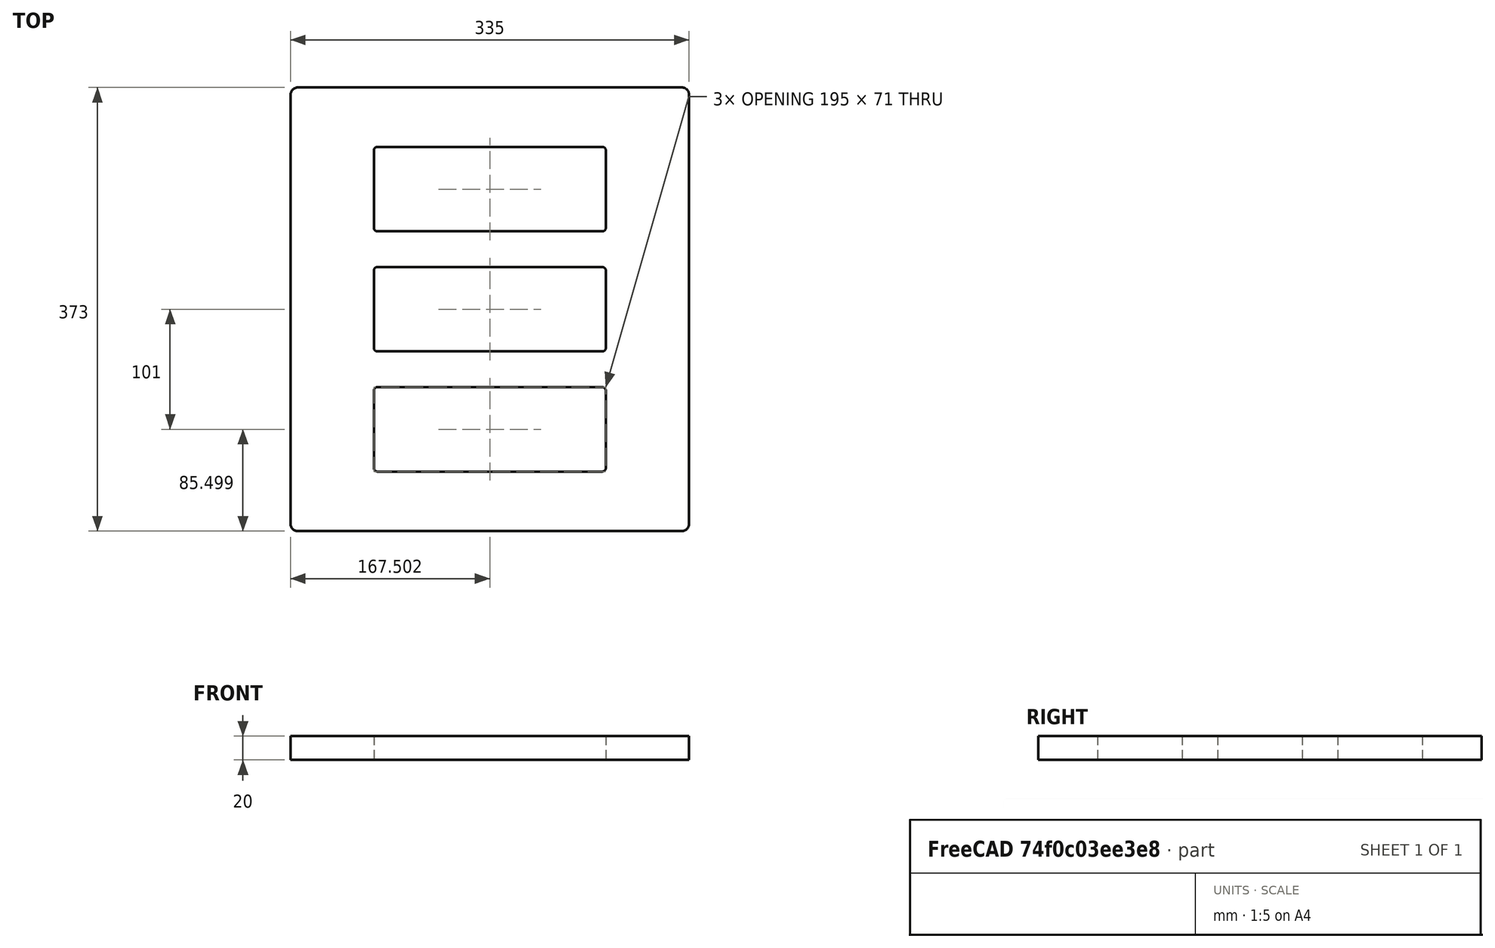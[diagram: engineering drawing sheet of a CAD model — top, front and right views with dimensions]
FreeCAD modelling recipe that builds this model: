
FCSTD DOCUMENT  (FreeCAD 0.16R6706 (Git))
Label: model
License: All rights reserved
LicenseURL: http://en.wikipedia.org/wiki/All_rights_reserved
objects: Sketcher::SketchObject×1, PartDesign::Pad×1
note: 3 computed .brp shape members not serialized (recipe doc carries the construction recipe); baked Part::Feature solids carry a one-line shape summary decoded from their .brp

FEATURE [Sketcher::SketchObject] Sketch002
  sketch-geometry (32):
    g0: LineSegment StartX=78.4625 StartY=-38.9411 StartZ=0 EndX=267.462 EndY=-38.9411 EndZ=0
    g1: LineSegment StartX=270.462 StartY=-41.9411 StartZ=0 EndX=270.462 EndY=-106.941 EndZ=0
    g2: LineSegment StartX=267.462 StartY=-109.941 StartZ=0 EndX=78.4625 EndY=-109.941 EndZ=0
    g3: LineSegment StartX=75.4625 StartY=-106.941 StartZ=0 EndX=75.4625 EndY=-41.9411 EndZ=0
    g4: LineSegment StartX=11.4625 StartY=11.0589 StartZ=0 EndX=334.462 EndY=11.0589 EndZ=0
    g5: LineSegment StartX=340.462 StartY=5.05895 StartZ=0 EndX=340.462 EndY=-355.941 EndZ=0
    g6: LineSegment StartX=334.462 StartY=-361.941 StartZ=0 EndX=11.4625 EndY=-361.941 EndZ=0
    g7: LineSegment StartX=5.46248 StartY=-355.941 StartZ=0 EndX=5.46248 EndY=5.05895 EndZ=0
    g8: ArcOfCircle CenterX=78.4625 CenterY=-41.9411 CenterZ=0 NormalX=0 NormalY=0 NormalZ=1 Radius=3 StartAngle=1.5708 EndAngle=3.14159
    g9: ArcOfCircle CenterX=78.4625 CenterY=-106.941 CenterZ=0 NormalX=0 NormalY=0 NormalZ=1 Radius=3 StartAngle=3.14159 EndAngle=4.71239
    g10: ArcOfCircle CenterX=267.462 CenterY=-106.941 CenterZ=0 NormalX=0 NormalY=0 NormalZ=1 Radius=3 StartAngle=4.71239 EndAngle=6.28319
    g11: ArcOfCircle CenterX=267.462 CenterY=-41.9411 CenterZ=0 NormalX=0 NormalY=0 NormalZ=1 Radius=3 StartAngle=0 EndAngle=1.5708
    g12: ArcOfCircle CenterX=334.462 CenterY=5.05895 CenterZ=0 NormalX=0 NormalY=0 NormalZ=1 Radius=6 StartAngle=0 EndAngle=1.5708
    g13: ArcOfCircle CenterX=11.4625 CenterY=5.05895 CenterZ=0 NormalX=0 NormalY=0 NormalZ=1 Radius=6 StartAngle=1.5708 EndAngle=3.14159
    g14: ArcOfCircle CenterX=11.4625 CenterY=-355.941 CenterZ=0 NormalX=0 NormalY=0 NormalZ=1 Radius=6 StartAngle=3.14159 EndAngle=4.71239
    g15: ArcOfCircle CenterX=334.462 CenterY=-355.941 CenterZ=0 NormalX=0 NormalY=0 NormalZ=1 Radius=6 StartAngle=4.71239 EndAngle=6.28319
    g16: LineSegment StartX=78.4625 StartY=-139.941 StartZ=0 EndX=267.462 EndY=-139.941 EndZ=0
    g17: LineSegment StartX=270.462 StartY=-142.941 StartZ=0 EndX=270.462 EndY=-207.941 EndZ=0
    g18: LineSegment StartX=267.462 StartY=-210.941 StartZ=0 EndX=78.4625 EndY=-210.941 EndZ=0
    g19: LineSegment StartX=75.4625 StartY=-207.941 StartZ=0 EndX=75.4625 EndY=-142.941 EndZ=0
    g20: LineSegment StartX=78.4625 StartY=-240.941 StartZ=0 EndX=267.462 EndY=-240.941 EndZ=0
    g21: LineSegment StartX=270.462 StartY=-243.941 StartZ=0 EndX=270.462 EndY=-308.941 EndZ=0
    g22: LineSegment StartX=267.462 StartY=-311.941 StartZ=0 EndX=78.4625 EndY=-311.941 EndZ=0
    g23: LineSegment StartX=75.4625 StartY=-308.941 StartZ=0 EndX=75.4625 EndY=-243.941 EndZ=0
    g24: ArcOfCircle CenterX=267.462 CenterY=-142.941 CenterZ=0 NormalX=0 NormalY=0 NormalZ=1 Radius=3 StartAngle=0 EndAngle=1.5708
    g25: ArcOfCircle CenterX=78.4625 CenterY=-142.941 CenterZ=0 NormalX=0 NormalY=0 NormalZ=1 Radius=3 StartAngle=1.5708 EndAngle=3.14159
    g26: ArcOfCircle CenterX=78.4625 CenterY=-207.941 CenterZ=0 NormalX=0 NormalY=0 NormalZ=1 Radius=3 StartAngle=3.14159 EndAngle=4.71239
    g27: ArcOfCircle CenterX=267.462 CenterY=-207.941 CenterZ=0 NormalX=0 NormalY=0 NormalZ=1 Radius=3 StartAngle=4.71239 EndAngle=6.28319
    g28: ArcOfCircle CenterX=267.462 CenterY=-243.941 CenterZ=0 NormalX=0 NormalY=0 NormalZ=1 Radius=3 StartAngle=0 EndAngle=1.5708
    g29: ArcOfCircle CenterX=267.462 CenterY=-308.941 CenterZ=0 NormalX=0 NormalY=0 NormalZ=1 Radius=3 StartAngle=4.71239 EndAngle=6.28319
    g30: ArcOfCircle CenterX=78.4625 CenterY=-308.941 CenterZ=0 NormalX=0 NormalY=0 NormalZ=1 Radius=3 StartAngle=3.14159 EndAngle=4.71239
    g31: ArcOfCircle CenterX=78.4625 CenterY=-243.941 CenterZ=0 NormalX=0 NormalY=0 NormalZ=1 Radius=3 StartAngle=1.5708 EndAngle=3.14159
  constraints (78):
    c: Horizontal(g0)
    c: Horizontal(g2)
    c: Vertical(g1)
    c: Vertical(g3)
    c: Horizontal(g4)
    c: Horizontal(g6)
    c: Vertical(g5)
    c: Vertical(g7)
    c: Tangent(g3,g8) = 1.5708
    c: Tangent(g0,g8) = 1.5708
    c: Tangent(g3,g9) = 1.5708
    c: Tangent(g2,g9) = 1.5708
    c: Tangent(g2,g10) = 1.5708
    c: Tangent(g1,g10) = 1.5708
    c: Tangent(g1,g11) = 1.5708
    c: Tangent(g0,g11) = 1.5708
    c: Distance(g3,g1) = 195
    c: Distance(g2,g0) = 71
    c: Tangent(g4,g12) = 1.5708
    c: Tangent(g5,g12) = 1.5708
    c: Tangent(g4,g13) = 1.5708
    c: Tangent(g7,g13) = 1.5708
    c: Tangent(g7,g14) = 1.5708
    c: Tangent(g6,g14) = 1.5708
    c: Tangent(g6,g15) = 1.5708
    c: Tangent(g5,g15) = 1.5708
    c: Radius(g15) = 6
    c: Equal(g15,g14)
    c: Equal(g15,g12)
    c: Equal(g15,g13)
    c: Radius(g11) = 3
    c: Equal(g11,g8)
    c: Equal(g11,g10)
    c: Equal(g11,g9)
    c: Distance(g3,g7) = 70
    c: Distance(g1,g5) = 70
    c: Distance(g0,g4) = 50
    c: Horizontal(g16)
    c: Horizontal(g18)
    c: Vertical(g17)
    c: Vertical(g19)
    c: Horizontal(g20)
    c: Horizontal(g22)
    c: Vertical(g21)
    c: Vertical(g23)
    c: Tangent(g17,g24) = 1.5708
    c: Tangent(g16,g24) = 1.5708
    c: Tangent(g16,g25) = 1.5708
    c: Tangent(g19,g25) = 1.5708
    c: Tangent(g19,g26) = 1.5708
    c: Tangent(g18,g26) = 1.5708
    c: Tangent(g18,g27) = 1.5708
    c: Tangent(g17,g27) = 1.5708
    c: Tangent(g20,g28) = 1.5708
    c: Tangent(g21,g28) = 1.5708
    c: Tangent(g21,g29) = 1.5708
    c: Tangent(g22,g29) = 1.5708
    c: Tangent(g22,g30) = 1.5708
    c: Tangent(g23,g30) = 1.5708
    c: Tangent(g23,g31) = 1.5708
    c: Tangent(g20,g31) = 1.5708
    c: Equal(g31,g30)
    c: Equal(g30,g29)
    c: Equal(g29,g28)
    c: Equal(g28,g27)
    c: Equal(g27,g24)
    c: Equal(g24,g25)
    c: Equal(g25,g26)
    c: Equal(g26,g11)
    c: Equal(g16,g0)
    c: Equal(g0,g20)
    c: Equal(g21,g17)
    c: Equal(g17,g1)
    c: Distance(g22,g6) = 50
    c: Distance(g2,g16) = 30
    c: Distance(g18,g20) = 30
    c: DistanceX(g19,g3) = 0
    c: DistanceX(g23,g19) = 0
FEATURE [PartDesign::Pad] Pad002  label="Фанера1"
  Length = 20
  Length2 = 100
  Reversed = true
  Sketch = -> Sketch002
  Type = 0
